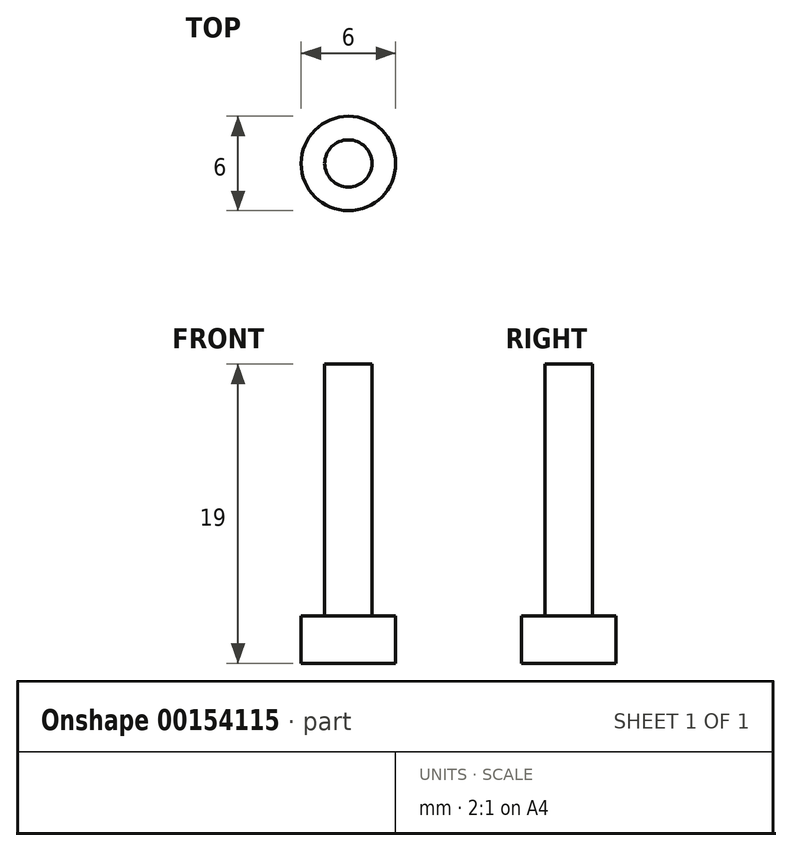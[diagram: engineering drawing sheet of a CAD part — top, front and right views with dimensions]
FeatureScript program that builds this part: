
annotation { "Feature Type Name" : "Feature", "Feature Type Description" : "" }
export const myFeature = defineFeature(function(context is Context, id is Id, definition is map)
    precondition{}
    {
        {
            var Q0;
            Q0=qCreatedBy(makeId("Front.planeOp"),FACE);
            var sketch = newSketch(context, id + "F0", { "sketchPlane" : qUnion([Q0])});
            skLineSegment(sketch, "E0", {"start": v(0, 0) * mm, "end": v(3, 0) * mm});
            skLineSegment(sketch, "E1", {"start": v(3, 0) * mm, "end": v(3, 3) * mm});
            skLineSegment(sketch, "E2", {"start": v(3, 3) * mm, "end": v(1.5, 3) * mm});
            skLineSegment(sketch, "E3", {"start": v(1.5, 3) * mm, "end": v(1.5, 19) * mm});
            skLineSegment(sketch, "E4", {"start": v(1.5, 19) * mm, "end": v(0, 19) * mm});
            skLineSegment(sketch, "E5", {"start": v(0, 19) * mm, "end": v(0, 0) * mm});
            skSolve(sketch);
        }
        {
            var Q0;
            Q0=makeQuery(id+"F0.imprint","IMPRINT",FACE,{"disambiguationData":[TD([[makeQuery(id+"F0.imprint","IMPRINT",EDGE,{"derivedFrom":sQuery(id+"F0.wireOp",EDGE,"E0")}),1.0]])]});
            var Q1;
            Q1=sQuery(id+"F0.wireOp",EDGE,"E5");
            revolve(context, id + "F1", {"entities" : qUnion([Q0]), "axis" : qUnion([Q1]), "revolveType" : RevolveType.FULL});
        }
    });
